# Revit family: Door_Coiling-Fabric_Dynaco_D4
name_source: partatom
category: Doors
units: mm (PartAtom-declared; Revit-internal decimal feet)

## family parameters
Always vertical = Yes
Classification Number = 23.30.10.17.27.11
Cut with Voids When Loaded = No
Host = Wall
Room Calculation Point = No
Shared = No

## types (8) — shared parameters
Analytic Construction = <None>
CAD Details = https://www.arcat.com
Define Thermal Properties by = Schematic Type
Fire Rating = as Specified
Function = Interior
Keynote = 08 34 00
Manufacturer = Dynaco/Entrematic
Maximum Size = 14' W x 14' H
Operating Speed = Opens at 78in / sec  ;  Closes at 24in / sec
Product Page URL = https://www.arcat.com
Rough Height = 0' - 0"
Rough Width = 0' - 0"
Specification = http://www.arcat.com
Thickness = 0' - 0"
URL = http://www.dynacodoor.us
Vision Lite Height = 1' - 3"
Wall Closure = By host

## per-type parameters (varying)
| type | Assembly Code | Description | Electrical_Phase | Model | Pressure Difference | Voltage Range |
| Exterior 575V 3 Phase | B2030410 | Dynaco Industrial Fabric Roll Up Door - Exterior D421 as Specified | 3 | D421 | Class II (60 MPH Winds) | 575 |
| Exterior 460V 3 Phase | B2030410 | Dynaco Industrial Fabric Roll Up Door - Exterior D421 as Specified | 3 | D421 | Class II (60 MPH Winds) | 460 |
| Exterior 208-230V 3 Phase | B2030410 | Dynaco Industrial Fabric Roll Up Door - Exterior D421 as Specified | 3 | D421 | Class II (60 MPH Winds) | 208-230 |
| Exterior 208-230V 1 Phase | B2030410 | Dynaco Industrial Fabric Roll Up Door - Exterior D421 as Specified | 1 | D421 | Class II (60 MPH Winds) | 208-230 |
| Interior 575V 3 Phase | C1020100 | Dynaco Industrial Fabric Roll Up Door - Interior D411 as Specified | 3 | D411 | Class I (50 MPH Winds) | 575 |
| Interior 460V 3 Phase | C1020100 | Dynaco Industrial Fabric Roll Up Door - Interior D411 as Specified | 3 | D411 | Class I (50 MPH Winds) | 460 |
| Interior 208-230V 3 Phase | C1020100 | Dynaco Industrial Fabric Roll Up Door - Interior D411 as Specified | 3 | D411 | Class I (50 MPH Winds) | 208-230 |
| Interior 208-230V 1 Phase | C1020100 | Dynaco Industrial Fabric Roll Up Door - Interior D411 as Specified | 1 | D411 | Class I (50 MPH Winds) | 208-230 |

## geometry (parser evidence)
native form markers: Sweep x5
no freeform markers — native parametric forms only
